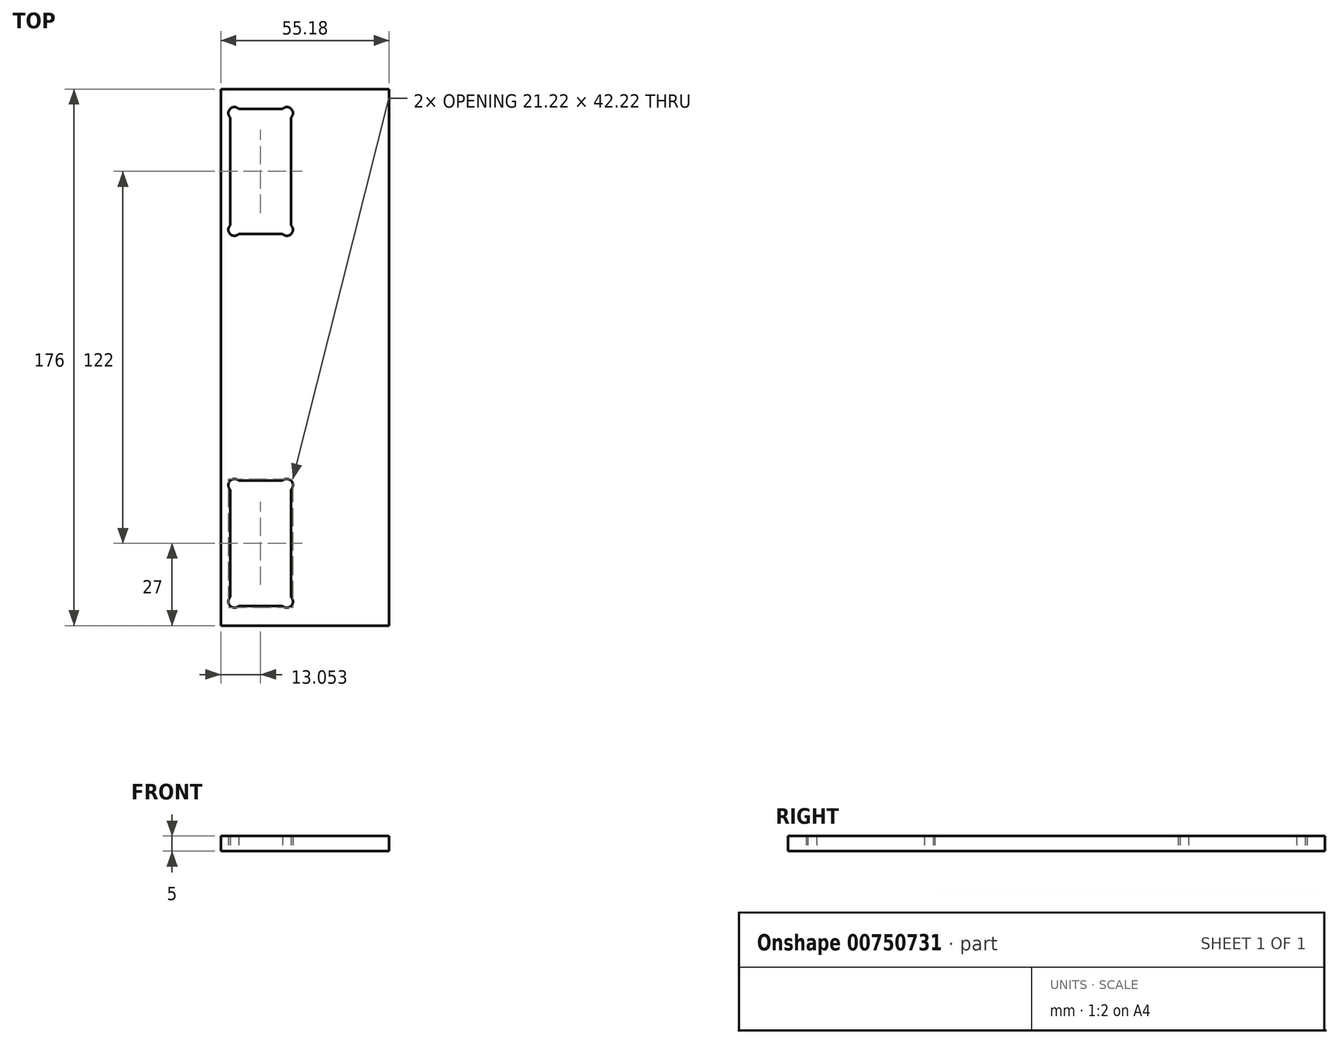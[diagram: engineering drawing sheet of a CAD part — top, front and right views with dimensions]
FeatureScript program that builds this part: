
annotation { "Feature Type Name" : "Feature", "Feature Type Description" : "" }
export const myFeature = defineFeature(function(context is Context, id is Id, definition is map)
    precondition{}
    {
        {
            var Q0;
            Q0=qCreatedBy(makeId("Top.planeOp"),FACE);
            var sketch = newSketch(context, id + "F0", { "sketchPlane" : qUnion([Q0])});
            skLineSegment(sketch, "E0.bottom", {"start": v(25.09, -88) * mm, "end": v(-25.09, -88) * mm, "construction": true});
            skLineSegment(sketch, "E0.top", {"start": v(25.09, 88) * mm, "end": v(-25.09, 88) * mm, "construction": true});
            skLineSegment(sketch, "E0.left", {"start": v(25.09, -88) * mm, "end": v(25.09, 88) * mm, "construction": true});
            skLineSegment(sketch, "E0.right", {"start": v(-25.09, -88) * mm, "end": v(-25.09, 88) * mm, "construction": true});
            skPoint(sketch, "E0.middle", {"position": v(0, 0) * mm});
            skLineSegment(sketch, "E1.bottom", {"start": v(-24.26, 81.23) * mm, "end": v(-4.81, 81.23) * mm, "construction": true});
            skLineSegment(sketch, "E1.top", {"start": v(-24.26, 55.78) * mm, "end": v(-4.81, 55.78) * mm, "construction": true});
            skLineSegment(sketch, "E1.left", {"start": v(-24.26, 81.23) * mm, "end": v(-24.26, 55.78) * mm, "construction": true});
            skLineSegment(sketch, "E1.right", {"start": v(-4.81, 81.23) * mm, "end": v(-4.81, 55.78) * mm, "construction": true});
            skLineSegment(sketch, "E2.bottom", {"start": v(27.59, -88) * mm, "end": v(-27.59, -88) * mm});
            skLineSegment(sketch, "E2.top", {"start": v(27.59, 88) * mm, "end": v(-27.59, 88) * mm});
            skLineSegment(sketch, "E2.left", {"start": v(27.59, -88) * mm, "end": v(27.59, 88) * mm});
            skLineSegment(sketch, "E2.right", {"start": v(-27.59, -88) * mm, "end": v(-27.59, 88) * mm});
            skLineSegment(sketch, "E3", {"start": v(-24.26, 68.5) * mm, "end": v(-4.81, 68.5) * mm, "construction": true});
            skPoint(sketch, "E4", {"position": v(-14.54, 68.5) * mm});
            skLineSegment(sketch, "E5", {"start": v(-14.54, 68.5) * mm, "end": v(-14.54, 0) * mm, "construction": true});
            skPoint(sketch, "E6", {"position": v(-14.54, 0) * mm});
            skLineSegment(sketch, "E7", {"start": v(-24.26, 55.78) * mm, "end": v(-24.26, 40.78) * mm, "construction": true});
            skLineSegment(sketch, "E8", {"start": v(-24.26, 40.78) * mm, "end": v(-4.81, 40.78) * mm, "construction": true});
            skLineSegment(sketch, "E9", {"start": v(-4.81, 40.78) * mm, "end": v(-4.81, 55.78) * mm, "construction": true});
            skLineSegment(sketch, "E10.0", {"start": v(-24.56, 81.53) * mm, "end": v(-24.56, 78.7) * mm, "construction": true});
            skLineSegment(sketch, "E10.1", {"start": v(-4.51, 81.53) * mm, "end": v(-4.51, 78.7) * mm, "construction": true});
            skLineSegment(sketch, "E10.2", {"start": v(-4.51, 40.48) * mm, "end": v(-4.51, 43.3) * mm, "construction": true});
            skLineSegment(sketch, "E10.3", {"start": v(-24.56, 81.53) * mm, "end": v(-21.73, 81.53) * mm, "construction": true});
            skLineSegment(sketch, "E10.4", {"start": v(-24.56, 40.48) * mm, "end": v(-21.73, 40.48) * mm, "construction": true});
            skLineSegment(sketch, "E10.5", {"start": v(-24.56, 55.78) * mm, "end": v(-24.56, 43.3) * mm});
            skArc(sketch, "E11", {"start": v(-21.73, 81.53) * mm, "mid": v(-24.56, 81.53) * mm, "end": v(-24.56, 78.7) * mm});
            skLineSegment(sketch, "E12", {"start": v(-23.15, 80.11) * mm, "end": v(-24.56, 81.53) * mm, "construction": true});
            skArc(sketch, "E13", {"start": v(-4.51, 78.7) * mm, "mid": v(-4.51, 81.53) * mm, "end": v(-7.34, 81.53) * mm});
            skArc(sketch, "E14", {"start": v(-7.34, 40.47) * mm, "mid": v(-4.51, 40.48) * mm, "end": v(-4.51, 43.3) * mm});
            skArc(sketch, "E15", {"start": v(-24.56, 43.3) * mm, "mid": v(-24.56, 40.48) * mm, "end": v(-21.73, 40.48) * mm});
            skLineSegment(sketch, "E16", {"start": v(-24.56, 40.48) * mm, "end": v(-23.15, 41.89) * mm, "construction": true});
            skLineSegment(sketch, "E17", {"start": v(-4.51, 40.48) * mm, "end": v(-5.93, 41.89) * mm, "construction": true});
            skLineSegment(sketch, "E18", {"start": v(-4.51, 81.53) * mm, "end": v(-5.93, 80.11) * mm, "construction": true});
            skLineSegment(sketch, "E19", {"start": v(-24.56, 78.7) * mm, "end": v(-24.56, 55.78) * mm});
            skLineSegment(sketch, "E20", {"start": v(-21.73, 81.53) * mm, "end": v(-7.34, 81.53) * mm});
            skLineSegment(sketch, "E21", {"start": v(-7.34, 81.53) * mm, "end": v(-4.51, 81.53) * mm, "construction": true});
            skLineSegment(sketch, "E22", {"start": v(-4.51, 78.7) * mm, "end": v(-4.51, 55.78) * mm});
            skLineSegment(sketch, "E23", {"start": v(-24.56, 43.3) * mm, "end": v(-24.56, 40.48) * mm, "construction": true});
            skLineSegment(sketch, "E24", {"start": v(-21.73, 40.48) * mm, "end": v(-7.34, 40.48) * mm});
            skLineSegment(sketch, "E25", {"start": v(-7.34, 40.48) * mm, "end": v(-4.51, 40.48) * mm, "construction": true});
            skLineSegment(sketch, "E26", {"start": v(-4.51, 43.3) * mm, "end": v(-4.51, 55.78) * mm});
            skLineSegment(sketch, "E27.MirrorCS", {"start": v(-21.73, -40.48) * mm, "end": v(-7.34, -40.48) * mm});
            skArc(sketch, "E28.MirrorCS", {"start": v(-24.56, -43.3) * mm, "mid": v(-24.56, -40.48) * mm, "end": v(-21.73, -40.48) * mm});
            skLineSegment(sketch, "E29.MirrorCS", {"start": v(-24.56, -55.78) * mm, "end": v(-24.56, -43.3) * mm});
            skArc(sketch, "E30.MirrorCS", {"start": v(-7.34, -40.47) * mm, "mid": v(-4.51, -40.48) * mm, "end": v(-4.51, -43.3) * mm});
            skLineSegment(sketch, "E31.MirrorCS", {"start": v(-4.51, -43.3) * mm, "end": v(-4.51, -55.78) * mm});
            skArc(sketch, "E32.MirrorCS", {"start": v(-21.73, -81.53) * mm, "mid": v(-24.56, -81.53) * mm, "end": v(-24.56, -78.7) * mm});
            skLineSegment(sketch, "E33.MirrorCS", {"start": v(-21.73, -81.53) * mm, "end": v(-7.34, -81.53) * mm});
            skArc(sketch, "E34.MirrorCS", {"start": v(-4.51, -78.7) * mm, "mid": v(-4.51, -81.53) * mm, "end": v(-7.34, -81.53) * mm});
            skLineSegment(sketch, "E35.MirrorCS", {"start": v(-4.51, -78.7) * mm, "end": v(-4.51, -55.78) * mm});
            skLineSegment(sketch, "E36.MirrorCS", {"start": v(-24.56, -78.7) * mm, "end": v(-24.56, -55.78) * mm});
            skSolve(sketch);
        }
        {
            var Q0;
            Q0=qSketchRegion(id+"F0",true);
            extrude(context, id + "F1", {"entities" : qUnion([Q0]), "depth" : 5 * mm, "offsetDistance" : 25 * mm});
        }
    });
